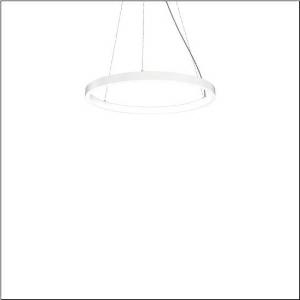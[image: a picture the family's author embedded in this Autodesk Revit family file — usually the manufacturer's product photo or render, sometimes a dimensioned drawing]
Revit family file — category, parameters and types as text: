
# Revit family: silica_r__21_ring-i_5pjbi2d1004a_0d30
name_source: partatom
category: Lighting Fixtures
units: mm (PartAtom-declared; Revit-internal decimal feet)

## family parameters
Cut with Voids When Loaded = No
Host = Face
Light Source = No
Part Type = Normal
Room Calculation Point = No
Round Connector Dimension = Use Diameter
Shared = No

## types (1)
- Silica® 21 Ring-I (1 x LED, 4800 lm, 80 W, 3000K)
    Apparent Load = 80 VA
    CIE Flux Codes = 22 48 76 50 101
    Color Rendering = 80
    Color Temperature = 3000K
    Default Elevation = 1800 mm
    Description = Silica® 21 Ring-I, suspended luminaire, of PMMA, frosted, light emission: inner ring side luminous distribution, primary light characteristic: symmetric, installation type: suspended mounting, LED, rated luminous flux: 4.800lm, luminous efficacy: 60lm/W, light colour: 830, colour temperature: 3000K, control gear: DALI 2, with terminal, 5-pole, mains connection: 230V, AC/DC, 0/50..60Hz, rated input power: 80W, housing, of extruded aluminium section, traffic white (RAL 9016), diameter: 805mm, ceiling canopy, traffic white (RAL 9016), protection rating (lamp compartment): IP40, insulation class (complete): insulation class I (protective earthing), certification: CE, impact resistance: IK02, permissible operating ambient temperature: 0..+35°C, packaging unit: 1 piece
    Height = 48 mm  [stored 0.15748 ft]
    Lamp = 1 x LED
    Lamp Light Flux = 4800 lm
    Lamp Power = 80 W
    Lamp count = 1
    Length = 805 mm
    Luminous efficacy = 60 lm/W
    Manufacturer = Siteco
    ModVariant = No
    Model = 5PJBI2D1004A
    Mounting Place = Ceiling
    Mounting Type = Pendant
    Number of Poles = 1
    OnlyDefault = Yes
    Power Factor = 1
    Product Name = Silica® 21 Ring-I
    Product group = suspended luminaire
    ProductGroupID = 905
    Protection Class = Protection class I
    Protection Degree = IP 40
    RLX_Detail_Level = 1
    RLX_Emergency_Light_Flux = 0 lm
    RLX_Emergency_Type = 0
    RLX_Emergency_Type_DB = No
    RlxData = <blob elided: 11597 chars, md5=c7e0d46d>
    Socket = socket
    Standby Power = 0 W
    System Light Flux = 4800 lm
    System Power = 80 W
    Type Comments = Product without accessories
    Type Image = l_1258367.jpg
    URL = http://relux.com
    VarID = ---
    Voltage = 0 V
    Weight = 0.00 kg
    Width = 0 mm  [stored 0 ft]

note: [stored X ft] marks values corroborated as IEEE doubles in the binary element streams (Revit-internal decimal feet)

## geometry (parser evidence)
native form markers: Sweep x10
no freeform markers — native parametric forms only
